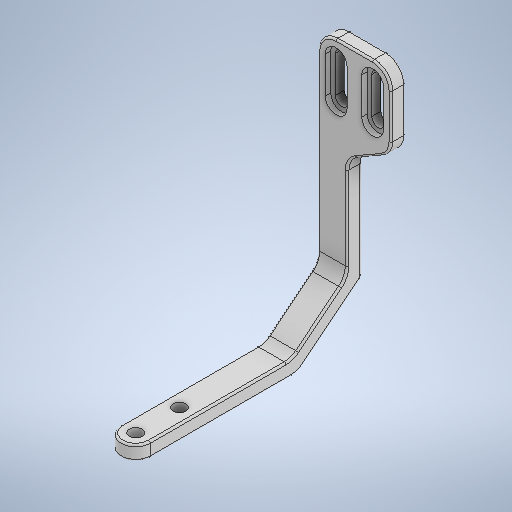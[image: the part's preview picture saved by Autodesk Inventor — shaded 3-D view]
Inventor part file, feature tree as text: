
AUTODESK INVENTOR PART (.ipt)
format: ipt  version: 2025.1 (Build 291241000, 241)  size: 431,104 bytes
history: native  units: mm
features: sketch x7, extrude x6, fillet x5, chamfer x2, projected_geometry x2
ambient origin geometry x8: Origin, YZ Plane, XZ Plane, XY Plane, X Axis, Y Axis, Z Axis, Center Point
bodies: Solid1 (feature_tree)
feature tree (22):
  extrude  "Extrusion1"  Depth=10.0mm
  chamfer  "Chamfer1"  Distance=8.0mm
  chamfer  "Chamfer2"  Distance=10.0mm
  fillet  "Fillet5"  Radius=1.5mm
  fillet  "Fillet6"  Radius=1.75mm
  extrude  "Extrusion5"  Depth=1.75mm
  extrude  "Extrusion2"  TaperAngle=0.0deg  [1 undecoded]
  extrude  "Extrusion3"  Depth=12.0mm
  extrude  "Extrusion4"  Depth=3.5mm
  fillet  "Fillet2"  [1 undecoded]
  fillet  "Fillet3"  Radius=4.0mm
  fillet  "Fillet4"  Radius=4.0mm
  extrude  "Extrusion6"  Depth=20.0mm
  sketch  "Sketch8"  dims[d12=5.0mm d13=10.0mm d14=1.5mm d15=0.0mm d16=1.75mm d17=1.75mm d18=0.0mm d19=0.0mm d20=12.0mm d21=3.5mm d26=0.0mm d27=0.0mm d29=4.0mm d30=4.0mm d31=20.0mm d32=20.0mm d33=60.0deg d34=8.0mm d35=0.0mm d36=4.0mm d37=5.0mm d38=0.5mm d39=5.7mm d40=1.5mm d41=0.0mm d42=12.0mm d43=15.0mm d44=45.0deg d45=17.5mm d46=14.0mm d47=45.0deg d48=5.0mm d49=1.0mm]
  sketch  "Sketch1"  dims[d0=10.0mm d2=57.0mm]
  sketch  "Sketch3"  dims[d3=62.0mm]
  sketch  "Sketch4"  dims[d4=4.0mm]
  projected_geometry  "Projected Loop1"
  projected_geometry  "Projected Loop2"
  sketch  "Sketch5"  dims[d5=4.0mm d6=8.0mm d7=0.0mm]
  sketch  "Sketch6"  dims[d10=3.0mm]
  sketch  "Sketch7"  dims[d11=10.0mm]
note: 2 required parameter values undecoded (feature->parameter linkage not recoverable at this tier; creation-order binding heuristic only, values carry confidence <= 0.55)
